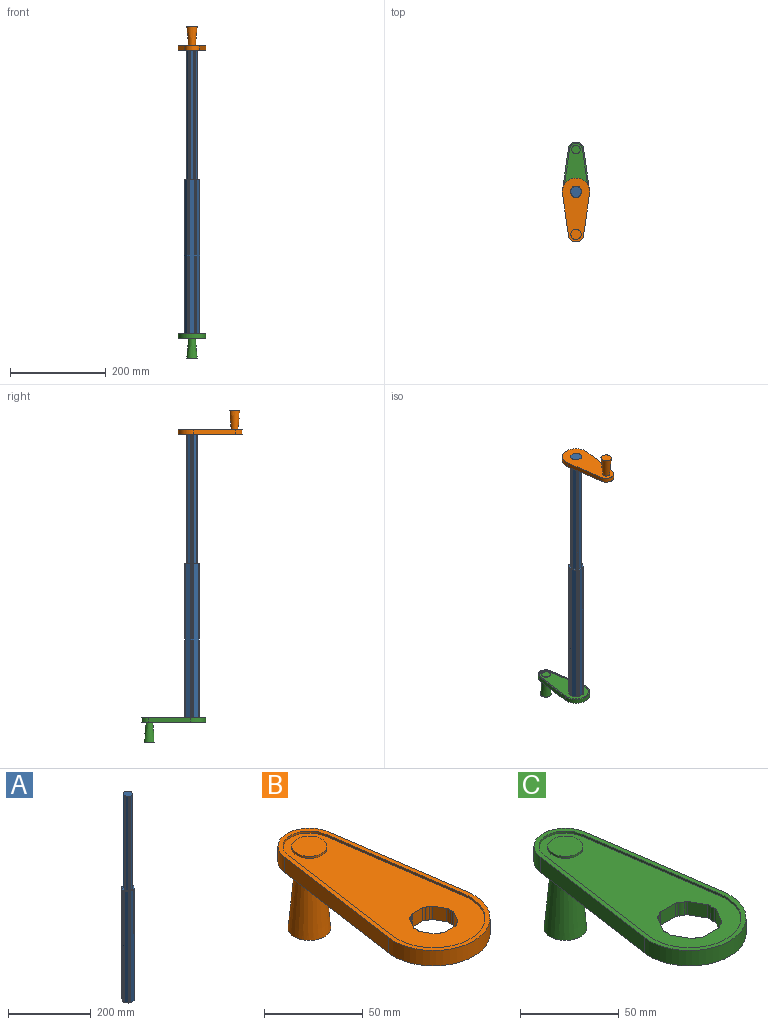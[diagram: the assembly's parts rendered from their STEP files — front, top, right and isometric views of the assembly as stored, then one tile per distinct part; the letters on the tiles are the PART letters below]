
ASSEMBLY  parts=3 mates=2
PART A: 51 faces, bbox 31.5x29.7x609.6 mm
  f0: plane 279.4x6.69mm, normal (-0.87,-0.5,0), area 2157.9mm2, adj f12,f13,f24,f37
  f1: cylinder r=3.17mm len=279.4mm, axis (0,0,-1), area 619.1mm2, adj f12,f13,f14,f37
  f2: plane 279.4x7.72mm, normal (0,-1,0), area 2157.9mm2, adj f12,f14,f15,f37
  f3: cylinder r=3.17mm len=279.4mm, axis (0,0,-1), area 619.1mm2, adj f12,f15,f16,f37
  f4: plane 279.4x6.69mm, normal (0.87,-0.5,0), area 2157.9mm2, adj f12,f16,f17,f37
  f5: cylinder r=3.17mm len=279.4mm, axis (0,0,-1), area 619.1mm2, adj f12,f17,f18,f37
  f6: plane 279.4x6.69mm, normal (0.87,0.5,0), area 2157.9mm2, adj f12,f18,f19,f37
  f7: cylinder r=3.17mm len=279.4mm, axis (0,0,-1), area 619.1mm2, adj f12,f19,f20,f37
  f8: plane 279.4x7.72mm, normal (0,1,0), area 2157.9mm2, adj f12,f20,f21,f37
  f9: cylinder r=3.17mm len=279.4mm, axis (0,0,-1), area 619.1mm2, adj f12,f21,f22,f37
  f10: plane 279.4x6.69mm, normal (-0.87,0.5,0), area 2157.9mm2, adj f12,f22,f23,f37
  f11: cylinder r=3.17mm len=279.4mm, axis (0,0,-1), area 619.1mm2, adj f12,f23,f24,f37
  f12: plane 23.25x22mm, normal (0,0,1), area 404.1mm2, adj f0,f1,f2,f3,f4,f5,f6,f7
  f13: cylinder r=1.27mm len=279.4mm, axis (0,0,-1), area 309.6mm2, adj f0,f1,f12,f37
  f14: cylinder r=1.27mm len=279.4mm, axis (0,0,-1), area 309.6mm2, adj f1,f2,f12,f37
  f15: cylinder r=1.27mm len=279.4mm, axis (0,0,-1), area 309.6mm2, adj f2,f3,f12,f37
  f16: cylinder r=1.27mm len=279.4mm, axis (0,0,-1), area 309.6mm2, adj f3,f4,f12,f37
  f17: cylinder r=1.27mm len=279.4mm, axis (0,0,-1), area 309.6mm2, adj f4,f5,f12,f37
  f18: cylinder r=1.27mm len=279.4mm, axis (0,0,-1), area 309.6mm2, adj f5,f6,f12,f37
  f19: cylinder r=1.27mm len=279.4mm, axis (0,0,-1), area 309.6mm2, adj f6,f7,f12,f37
  f20: cylinder r=1.27mm len=279.4mm, axis (0,0,-1), area 309.6mm2, adj f7,f8,f12,f37
  f21: cylinder r=1.27mm len=279.4mm, axis (0,0,-1), area 309.6mm2, adj f8,f9,f12,f37
  f22: cylinder r=1.27mm len=279.4mm, axis (0,0,-1), area 309.6mm2, adj f9,f10,f12,f37
  f23: cylinder r=1.27mm len=279.4mm, axis (0,0,-1), area 309.6mm2, adj f10,f11,f12,f37
  f24: cylinder r=1.27mm len=279.4mm, axis (0,0,-1), area 309.6mm2, adj f0,f11,f12,f37
  f25: plane 330.2x9.4mm, normal (-0.87,-0.5,0), area 3583mm2, adj f37,f38,f49,f50
  f26: cylinder r=4.29mm len=330.2mm, axis (0,0,-1), area 1091.8mm2, adj f37,f38,f39,f50
  f27: plane 330.2x10.85mm, normal (0,-1,0), area 3583mm2, adj f37,f39,f40,f50
  f28: cylinder r=4.29mm len=330.2mm, axis (0,0,-1), area 1091.8mm2, adj f37,f40,f41,f50
  f29: plane 330.2x9.4mm, normal (0.87,-0.5,0), area 3583mm2, adj f37,f41,f42,f50
  f30: cylinder r=4.29mm len=330.2mm, axis (0,0,-1), area 1091.8mm2, adj f37,f42,f43,f50
  f31: plane 330.2x9.4mm, normal (0.87,0.5,0), area 3583mm2, adj f37,f43,f44,f50
  f32: cylinder r=4.29mm len=330.2mm, axis (0,0,-1), area 1091.8mm2, adj f37,f44,f45,f50
  f33: plane 330.2x10.85mm, normal (0,1,0), area 3583mm2, adj f37,f45,f46,f50
  f34: cylinder r=4.29mm len=330.2mm, axis (0,0,-1), area 1091.8mm2, adj f37,f46,f47,f50
  f35: plane 330.2x9.4mm, normal (-0.87,0.5,0), area 3583mm2, adj f37,f47,f48,f50
  f36: cylinder r=4.29mm len=330.2mm, axis (0,0,-1), area 1091.8mm2, adj f37,f48,f49,f50
  f37: plane 31.48x29.7mm, normal (0,0,1), area 332.9mm2, adj f0,f1,f2,f3,f4,f5,f6,f7
  f38: cylinder r=1.27mm len=330.2mm, axis (0,0,-1), area 381.3mm2, adj f25,f26,f37,f50
  f39: cylinder r=1.27mm len=330.2mm, axis (0,0,-1), area 381.3mm2, adj f26,f27,f37,f50
  f40: cylinder r=1.27mm len=330.2mm, axis (0,0,-1), area 381.3mm2, adj f27,f28,f37,f50
  f41: cylinder r=1.27mm len=330.2mm, axis (0,0,-1), area 381.3mm2, adj f28,f29,f37,f50
  f42: cylinder r=1.27mm len=330.2mm, axis (0,0,-1), area 381.3mm2, adj f29,f30,f37,f50
  f43: cylinder r=1.27mm len=330.2mm, axis (0,0,-1), area 381.3mm2, adj f30,f31,f37,f50
  f44: cylinder r=1.27mm len=330.2mm, axis (0,0,-1), area 381.3mm2, adj f31,f32,f37,f50
  f45: cylinder r=1.27mm len=330.2mm, axis (0,0,-1), area 381.3mm2, adj f32,f33,f37,f50
  f46: cylinder r=1.27mm len=330.2mm, axis (0,0,-1), area 381.3mm2, adj f33,f34,f37,f50
  f47: cylinder r=1.27mm len=330.2mm, axis (0,0,-1), area 381.3mm2, adj f34,f35,f37,f50
  f48: cylinder r=1.27mm len=330.2mm, axis (0,0,-1), area 381.3mm2, adj f35,f36,f37,f50
  f49: cylinder r=1.27mm len=330.2mm, axis (0,0,-1), area 381.3mm2, adj f25,f36,f37,f50
  f50: plane 31.48x29.7mm, normal (0,0,-1), area 737mm2, adj f25,f26,f27,f28,f29,f30,f31,f32
PART B: 39 faces, bbox 57.2x133.4x50.8 mm
  f0: plane 133.35x57.15mm, normal (0,0,-1), area 5066.4mm2, adj f2,f3,f4,f5,f14,f15,f16,f17
  f1: plane 17.78x17.78mm, normal (0,0,1), area 248.3mm2, adj f10
  f2: cylinder r=28.57mm len=57.15mm, axis (0,0,-1), area 933.1mm2, adj f0,f3,f5,f6
  f3: plane 87.09x12.57mm, normal (0.99,0.14,0), area 838.1mm2, adj f0,f2,f4,f6
  f4: cylinder r=15.88mm len=31.42mm, axis (0,0,-1), area 431.7mm2, adj f0,f3,f5,f6
  f5: plane 87.09x12.57mm, normal (-0.99,0.14,0), area 838.1mm2, adj f0,f2,f4,f6
  f6: plane 133.35x57.15mm, normal (0,0,1), area 790.7mm2, adj f2,f3,f4,f5,f7,f8,f9,f11
  f7: plane 87.09x12.57mm, normal (0.99,-0.14,0), area 111.7mm2, adj f6,f8,f11,f12
  f8: cylinder r=26.04mm len=52.07mm, axis (0,0,1), area 113.4mm2, adj f6,f7,f9,f12
  f9: plane 87.09x12.57mm, normal (-0.99,-0.14,0), area 111.7mm2, adj f6,f8,f11,f12
  f10: cylinder r=8.89mm len=17.78mm, axis (0,0,1), area 70.9mm2, adj f1,f12
  f11: cylinder r=13.33mm len=26.4mm, axis (0,0,1), area 48.3mm2, adj f6,f7,f9,f12
  f12: plane 128.27x52.07mm, normal (0,0,1), area 4189.5mm2, adj f7,f8,f9,f10,f11,f15,f16,f17
  f13: plane 21.59x21.59mm, normal (0,0,-1), area 366.1mm2, adj f14
  f14: cone r=6.35mm half-angle=5deg, axis (0,0,-1), area 2340.1mm2, adj f0,f13
  f15: plane 8.26x6.69mm, normal (0.87,0.5,0), area 63.8mm2, adj f0,f12,f27,f38
  f16: cylinder r=2.67mm len=8.26mm, axis (0,0,-1), area 15.4mm2, adj f0,f12,f27,f28
  f17: plane 8.26x7.72mm, normal (0,1,0), area 63.8mm2, adj f0,f12,f28,f29
  f18: cylinder r=2.67mm len=8.26mm, axis (0,0,-1), area 15.4mm2, adj f0,f12,f29,f30
  f19: plane 8.26x6.69mm, normal (-0.87,0.5,0), area 63.8mm2, adj f0,f12,f30,f31
  f20: cylinder r=2.67mm len=8.26mm, axis (0,0,-1), area 15.4mm2, adj f0,f12,f31,f32
  f21: plane 8.26x6.69mm, normal (-0.87,-0.5,0), area 63.8mm2, adj f0,f12,f32,f33
  f22: cylinder r=2.67mm len=8.26mm, axis (0,0,-1), area 15.4mm2, adj f0,f12,f33,f34
  f23: plane 8.26x7.72mm, normal (0,-1,0), area 63.8mm2, adj f0,f12,f34,f35
  f24: cylinder r=2.67mm len=8.26mm, axis (0,0,-1), area 15.4mm2, adj f0,f12,f35,f36
  f25: plane 8.26x6.69mm, normal (0.87,-0.5,0), area 63.8mm2, adj f0,f12,f36,f37
  f26: cylinder r=2.67mm len=8.26mm, axis (0,0,-1), area 15.4mm2, adj f0,f12,f37,f38
  f27: cylinder r=1.78mm len=8.26mm, axis (0,0,-1), area 12.8mm2, adj f0,f12,f15,f16
  f28: cylinder r=1.78mm len=8.26mm, axis (0,0,-1), area 12.8mm2, adj f0,f12,f16,f17
  f29: cylinder r=1.78mm len=8.26mm, axis (0,0,-1), area 12.8mm2, adj f0,f12,f17,f18
  f30: cylinder r=1.78mm len=8.26mm, axis (0,0,-1), area 12.8mm2, adj f0,f12,f18,f19
  f31: cylinder r=1.78mm len=8.26mm, axis (0,0,-1), area 12.8mm2, adj f0,f12,f19,f20
  f32: cylinder r=1.78mm len=8.26mm, axis (0,0,-1), area 12.8mm2, adj f0,f12,f20,f21
  f33: cylinder r=1.78mm len=8.26mm, axis (0,0,-1), area 12.8mm2, adj f0,f12,f21,f22
  f34: cylinder r=1.78mm len=8.26mm, axis (0,0,-1), area 12.8mm2, adj f0,f12,f22,f23
  f35: cylinder r=1.78mm len=8.26mm, axis (0,0,-1), area 12.8mm2, adj f0,f12,f23,f24
  f36: cylinder r=1.78mm len=8.26mm, axis (0,0,-1), area 12.8mm2, adj f0,f12,f24,f25
  f37: cylinder r=1.78mm len=8.26mm, axis (0,0,-1), area 12.8mm2, adj f0,f12,f25,f26
  f38: cylinder r=1.78mm len=8.26mm, axis (0,0,-1), area 12.8mm2, adj f0,f12,f15,f26
PART C: 39 faces, bbox 57.2x133.4x50.8 mm
  f0: plane 17.78x17.78mm, normal (0,0,1), area 248.3mm2, adj f10
  f1: cylinder r=28.57mm len=57.15mm, axis (0,0,-1), area 933.1mm2, adj f2,f4,f5,f6
  f2: plane 87.09x12.57mm, normal (0.99,0.14,0), area 838.1mm2, adj f1,f3,f5,f6
  f3: cylinder r=15.88mm len=31.42mm, axis (0,0,-1), area 431.7mm2, adj f2,f4,f5,f6
  f4: plane 87.09x12.57mm, normal (-0.99,0.14,0), area 838.1mm2, adj f1,f3,f5,f6
  f5: plane 133.35x57.15mm, normal (0,0,1), area 790.7mm2, adj f1,f2,f3,f4,f7,f8,f9,f11
  f6: plane 133.35x57.15mm, normal (0,0,-1), area 4720.3mm2, adj f1,f2,f3,f4,f14,f15,f16,f17
  f7: plane 87.09x12.57mm, normal (0.99,-0.14,0), area 111.7mm2, adj f5,f8,f11,f12
  f8: cylinder r=26.04mm len=52.07mm, axis (0,0,1), area 113.4mm2, adj f5,f7,f9,f12
  f9: plane 87.09x12.57mm, normal (-0.99,-0.14,0), area 111.7mm2, adj f5,f8,f11,f12
  f10: cylinder r=8.89mm len=17.78mm, axis (0,0,1), area 70.9mm2, adj f0,f12
  f11: cylinder r=13.33mm len=26.4mm, axis (0,0,1), area 48.3mm2, adj f5,f7,f9,f12
  f12: plane 128.27x52.07mm, normal (0,0,1), area 3843.5mm2, adj f7,f8,f9,f10,f11,f15,f16,f17
  f13: plane 21.59x21.59mm, normal (0,0,-1), area 366.1mm2, adj f14
  f14: cone r=6.35mm half-angle=5deg, axis (0,0,-1), area 2340.1mm2, adj f6,f13
  f15: plane 9.4x8.26mm, normal (0.87,0.5,0), area 89.6mm2, adj f6,f12,f27,f38
  f16: cylinder r=3.78mm len=8.26mm, axis (0,0,-1), area 24.1mm2, adj f6,f12,f27,f28
  f17: plane 10.85x8.26mm, normal (0,1,0), area 89.6mm2, adj f6,f12,f28,f29
  f18: cylinder r=3.78mm len=8.26mm, axis (0,0,-1), area 24.1mm2, adj f6,f12,f29,f30
  f19: plane 9.4x8.26mm, normal (-0.87,0.5,0), area 89.6mm2, adj f6,f12,f30,f31
  f20: cylinder r=3.78mm len=8.26mm, axis (0,0,-1), area 24.1mm2, adj f6,f12,f31,f32
  f21: plane 9.4x8.26mm, normal (-0.87,-0.5,0), area 89.6mm2, adj f6,f12,f32,f33
  f22: cylinder r=3.78mm len=8.26mm, axis (0,0,-1), area 24.1mm2, adj f6,f12,f33,f34
  f23: plane 10.85x8.26mm, normal (0,-1,0), area 89.6mm2, adj f6,f12,f34,f35
  f24: cylinder r=3.78mm len=8.26mm, axis (0,0,-1), area 24.1mm2, adj f6,f12,f35,f36
  f25: plane 9.4x8.26mm, normal (0.87,-0.5,0), area 89.6mm2, adj f6,f12,f36,f37
  f26: cylinder r=3.78mm len=8.26mm, axis (0,0,-1), area 24.1mm2, adj f6,f12,f37,f38
  f27: cylinder r=1.78mm len=8.26mm, axis (0,0,-1), area 13.3mm2, adj f6,f12,f15,f16
  f28: cylinder r=1.78mm len=8.26mm, axis (0,0,-1), area 13.3mm2, adj f6,f12,f16,f17
  f29: cylinder r=1.78mm len=8.26mm, axis (0,0,-1), area 13.3mm2, adj f6,f12,f17,f18
  f30: cylinder r=1.78mm len=8.26mm, axis (0,0,-1), area 13.3mm2, adj f6,f12,f18,f19
  f31: cylinder r=1.78mm len=8.26mm, axis (0,0,-1), area 13.3mm2, adj f6,f12,f19,f20
  f32: cylinder r=1.78mm len=8.26mm, axis (0,0,-1), area 13.3mm2, adj f6,f12,f20,f21
  f33: cylinder r=1.78mm len=8.26mm, axis (0,0,-1), area 13.3mm2, adj f6,f12,f21,f22
  f34: cylinder r=1.78mm len=8.26mm, axis (0,0,-1), area 13.3mm2, adj f6,f12,f22,f23
  f35: cylinder r=1.78mm len=8.26mm, axis (0,0,-1), area 13.3mm2, adj f6,f12,f23,f24
  f36: cylinder r=1.78mm len=8.26mm, axis (0,0,-1), area 13.3mm2, adj f6,f12,f24,f25
  f37: cylinder r=1.78mm len=8.26mm, axis (0,0,-1), area 13.3mm2, adj f6,f12,f25,f26
  f38: cylinder r=1.78mm len=8.26mm, axis (0,0,-1), area 13.3mm2, adj f6,f12,f15,f26
PLACE A at identity
PLACE B rot(axis=(1,0,0),180deg) t=(0,0,609.6)mm
PLACE C at identity
MATE fastened C.f1 <-> A.f50  axis (0,0,-1) through (0,0,0)mm
MATE fastened B.f2 <-> A.f12  axis (0,0,1) through (0,0,609.6)mm
